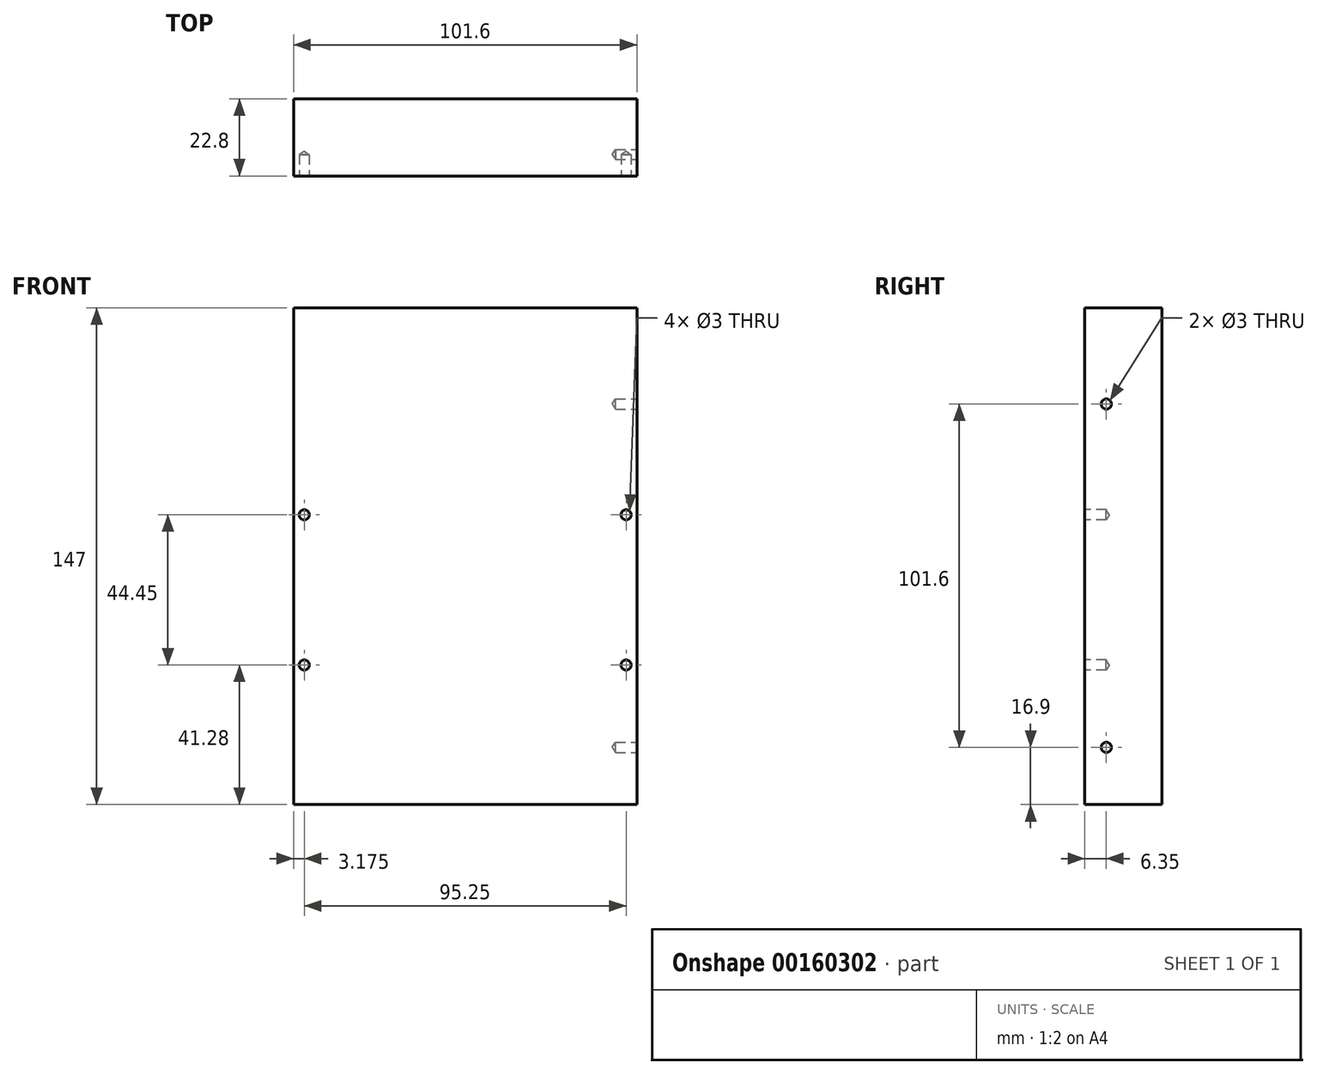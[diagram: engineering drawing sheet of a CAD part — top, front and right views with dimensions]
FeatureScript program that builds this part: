
annotation { "Feature Type Name" : "Feature", "Feature Type Description" : "" }
export const myFeature = defineFeature(function(context is Context, id is Id, definition is map)
    precondition{}
    {
        {
            var Q0;
            Q0=qCreatedBy(makeId("Front.planeOp"),FACE);
            var sketch = newSketch(context, id + "F0", { "sketchPlane" : qUnion([Q0])});
            skLineSegment(sketch, "E0.bottom", {"start": v(0, 0) * mm, "end": v(101.6, 0) * mm});
            skLineSegment(sketch, "E0.top", {"start": v(0, 147) * mm, "end": v(101.6, 147) * mm});
            skLineSegment(sketch, "E0.left", {"start": v(0, 0) * mm, "end": v(0, 147) * mm});
            skLineSegment(sketch, "E0.right", {"start": v(101.6, 0) * mm, "end": v(101.6, 147) * mm});
            skSolve(sketch);
        }
        {
            var Q0;
            Q0=makeQuery(id+"F0.imprint","IMPRINT",FACE,{"disambiguationData":[TD([[makeQuery(id+"F0.imprint","IMPRINT",EDGE,{"derivedFrom":sQuery(id+"F0.wireOp",EDGE,"E0.bottom")}),1.0]])]});
            extrude(context, id + "F1", {"entities" : qUnion([Q0]), "depth" : 22.8 * mm});
        }
        {
            var Q0;
            Q0=makeQuery(id+"F1.opExtrude","CAP_FACE",FACE,{"disambiguationData":[OSD([sQuery(id+"F0.wireOp",EDGE,"E0.bottom"),sQuery(id+"F0.wireOp",EDGE,"E0.top"),sQuery(id+"F0.wireOp",EDGE,"E0.left"),sQuery(id+"F0.wireOp",EDGE,"E0.right")])],"isStart":false});
            var sketch = newSketch(context, id + "F2", { "sketchPlane" : qUnion([Q0])});
            skPoint(sketch, "E1", {"position": v(3.17, 41.28) * mm});
            skPoint(sketch, "E2", {"position": v(3.17, 85.73) * mm});
            skLineSegment(sketch, "E3", {"start": v(50.8, 147) * mm, "end": v(50.8, 0) * mm, "construction": true});
            skPoint(sketch, "E4.MirrorP", {"position": v(98.42, 41.28) * mm});
            skPoint(sketch, "E5.MirrorP", {"position": v(98.42, 85.73) * mm});
            skSolve(sketch);
        }
        {
            var Q0;
            Q0=sQuery(id+"F2.wireOp",VERTEX,"E1");
            var Q1;
            Q1=sQuery(id+"F2.wireOp",VERTEX,"E2");
            var Q2;
            Q2=sQuery(id+"F2.wireOp",VERTEX,"E5.MirrorP");
            var Q3;
            Q3=sQuery(id+"F2.wireOp",VERTEX,"E4.MirrorP");
            var Q4;
            Q4=makeQuery(id+"F1.opExtrude","SWEPT_BODY",BODY,{"disambiguationData":[OSD([sQuery(id+"F0.wireOp",EDGE,"E0.bottom"),sQuery(id+"F0.wireOp",EDGE,"E0.top"),sQuery(id+"F0.wireOp",EDGE,"E0.left"),sQuery(id+"F0.wireOp",EDGE,"E0.right")])]});
            hole(context, id + "F3", {"style" : HoleStyle.SIMPLE, "endStyle" : HoleEndStyle.BLIND, "holeDiameter" : 3 * mm, "holeDepth" : 6.35 * mm, "locations" : qUnion([Q0, Q1, Q2, Q3]), "scope" : qUnion([Q4])});
        }
        {
            var Q0;
            Q0=makeQuery(id+"F1.opExtrude","SWEPT_FACE",FACE,{"disambiguationData":[OSD([sQuery(id+"F0.wireOp",EDGE,"E0.right")])]});
            var sketch = newSketch(context, id + "F4", { "sketchPlane" : qUnion([Q0])});
            skPoint(sketch, "E6", {"position": v(-16.45, 16.9) * mm});
            skPoint(sketch, "E7", {"position": v(-16.45, 118.5) * mm});
            skSolve(sketch);
        }
        {
            var Q0;
            Q0=sQuery(id+"F4.wireOp",VERTEX,"E7");
            var Q1;
            Q1=sQuery(id+"F4.wireOp",VERTEX,"E6");
            var Q2;
            Q2=makeQuery(id+"F1.opExtrude","SWEPT_BODY",BODY,{"disambiguationData":[OSD([sQuery(id+"F0.wireOp",EDGE,"E0.bottom"),sQuery(id+"F0.wireOp",EDGE,"E0.top"),sQuery(id+"F0.wireOp",EDGE,"E0.left"),sQuery(id+"F0.wireOp",EDGE,"E0.right")])]});
            hole(context, id + "F5", {"style" : HoleStyle.SIMPLE, "endStyle" : HoleEndStyle.BLIND, "holeDiameter" : 3 * mm, "holeDepth" : 6.35 * mm, "locations" : qUnion([Q0, Q1]), "scope" : qUnion([Q2])});
        }
        {
            var Q0;
            Q0=makeQuery(id+"F1.opExtrude","CAP_EDGE",EDGE,{"disambiguationData":[OSD([sQuery(id+"F0.wireOp",EDGE,"E0.bottom")])],"isStart":true});
            cPlane(context, id + "F6", {"entities" : qUnion([Q0]), "cplaneType" : CPlaneType.MID_PLANE, "offset" : 25 * mm, "width" : 150 * mm, "height" : 150 * mm});
        }
    });
